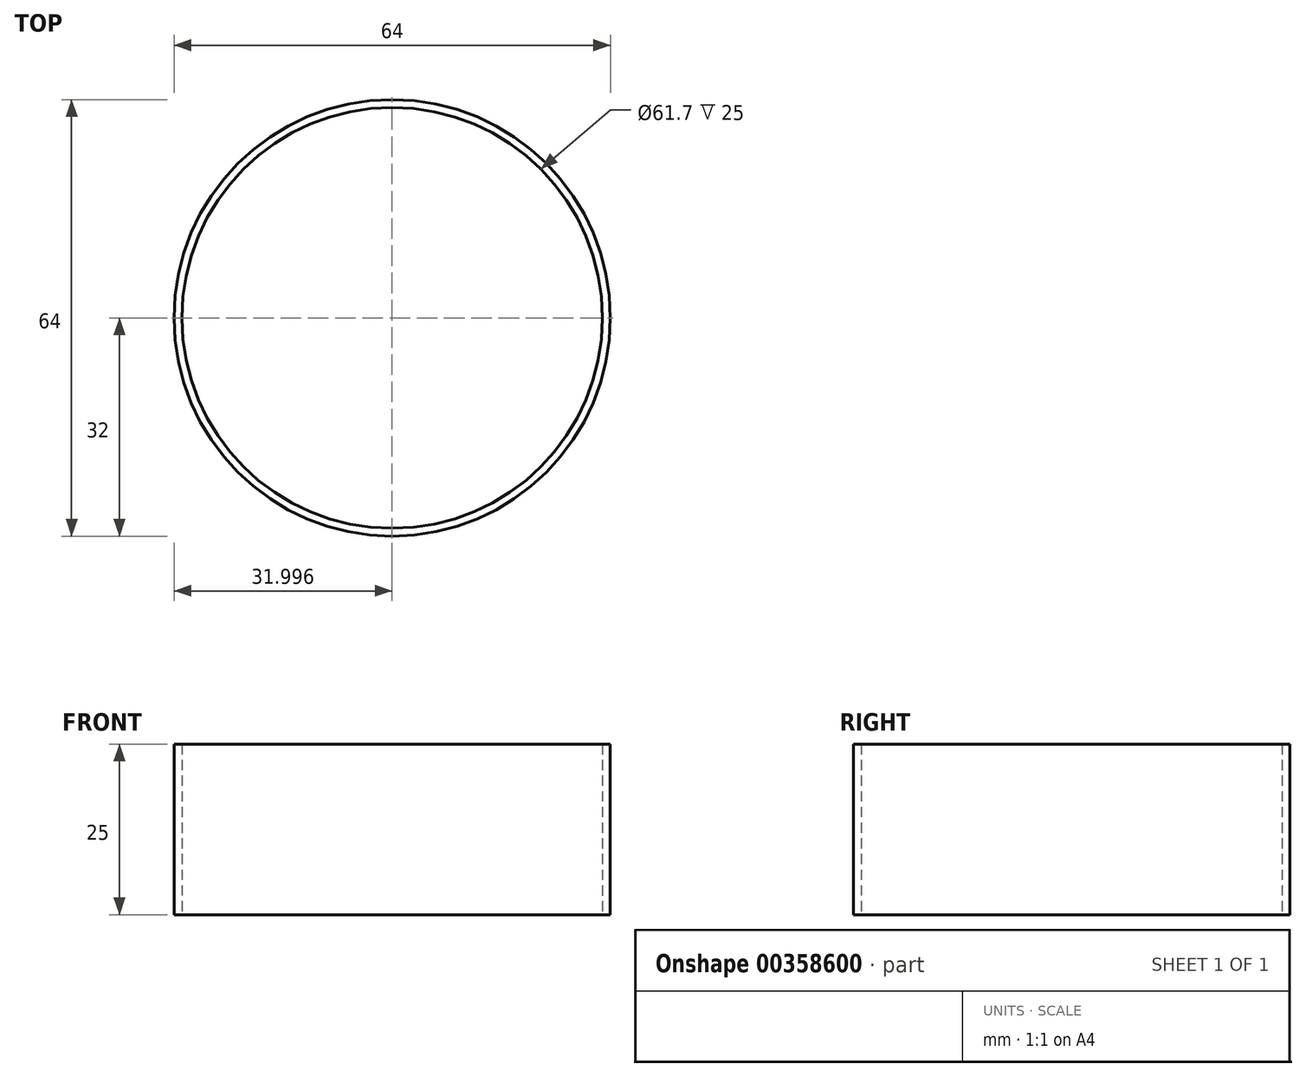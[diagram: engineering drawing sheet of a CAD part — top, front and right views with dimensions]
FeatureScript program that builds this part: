
annotation { "Feature Type Name" : "Feature", "Feature Type Description" : "" }
export const myFeature = defineFeature(function(context is Context, id is Id, definition is map)
    precondition{}
    {
        {
            var Q0;
            Q0=qCreatedBy(makeId("Top.planeOp"),FACE);
            var sketch = newSketch(context, id + "F0", { "sketchPlane" : qUnion([Q0])});
            skLineSegment(sketch, "E0", {"start": v(7.64, -19.63) * mm, "end": v(10.34, -16.68) * mm});
            skLineSegment(sketch, "E1", {"start": v(10.34, -16.68) * mm, "end": v(12.7, -18.83) * mm});
            skLineSegment(sketch, "E2", {"start": v(12.7, -18.83) * mm, "end": v(10, -21.79) * mm});
            skLineSegment(sketch, "E3", {"start": v(10, -21.79) * mm, "end": v(10.96, -22.66) * mm});
            skLineSegment(sketch, "E4", {"start": v(10.96, -22.66) * mm, "end": v(14.34, -18.97) * mm});
            skLineSegment(sketch, "E5", {"start": v(14.34, -18.97) * mm, "end": v(17.44, -21.8) * mm});
            skLineSegment(sketch, "E6", {"start": v(17.44, -21.8) * mm, "end": v(11.23, -28.6) * mm});
            skLineSegment(sketch, "E7", {"start": v(11.23, -28.6) * mm, "end": v(0.75, -19.02) * mm});
            skLineSegment(sketch, "E8", {"start": v(0.75, -19.02) * mm, "end": v(3.58, -15.92) * mm});
            skLineSegment(sketch, "E9", {"start": v(3.58, -15.92) * mm, "end": v(7.64, -19.63) * mm});
            skLineSegment(sketch, "E10", {"start": v(11.3, -18.9) * mm, "end": v(8.6, -21.85) * mm});
            skLineSegment(sketch, "E11", {"start": v(8.6, -21.85) * mm, "end": v(11.03, -24.08) * mm});
            skLineSegment(sketch, "E12", {"start": v(11.03, -24.08) * mm, "end": v(14.4, -20.39) * mm});
            skLineSegment(sketch, "E13", {"start": v(14.4, -20.39) * mm, "end": v(16.02, -21.87) * mm});
            skLineSegment(sketch, "E14", {"start": v(16.02, -21.87) * mm, "end": v(11.17, -27.18) * mm});
            skLineSegment(sketch, "E15", {"start": v(11.17, -27.18) * mm, "end": v(2.16, -18.95) * mm});
            skLineSegment(sketch, "E16", {"start": v(2.16, -18.95) * mm, "end": v(3.65, -17.33) * mm});
            skLineSegment(sketch, "E17", {"start": v(3.65, -17.33) * mm, "end": v(7.7, -21.04) * mm});
            skLineSegment(sketch, "E18", {"start": v(7.7, -21.04) * mm, "end": v(10.4, -18.09) * mm});
            skLineSegment(sketch, "E19", {"start": v(10.4, -18.09) * mm, "end": v(11.3, -18.9) * mm});
            skLineSegment(sketch, "E20", {"start": v(19.9, -16.36) * mm, "end": v(6.3, -12.26) * mm});
            skLineSegment(sketch, "E21", {"start": v(6.3, -12.26) * mm, "end": v(7.5, -8.24) * mm});
            skLineSegment(sketch, "E22", {"start": v(7.5, -8.24) * mm, "end": v(21.1, -12.34) * mm});
            skLineSegment(sketch, "E23", {"start": v(21.1, -12.34) * mm, "end": v(19.9, -16.36) * mm});
            skLineSegment(sketch, "E24", {"start": v(8.18, -9.49) * mm, "end": v(19.86, -13.01) * mm});
            skLineSegment(sketch, "E25", {"start": v(19.86, -13.01) * mm, "end": v(19.22, -15.12) * mm});
            skLineSegment(sketch, "E26", {"start": v(19.22, -15.12) * mm, "end": v(7.54, -11.6) * mm});
            skLineSegment(sketch, "E27", {"start": v(7.54, -11.6) * mm, "end": v(8.18, -9.49) * mm});
            skLineSegment(sketch, "E28", {"start": v(8.58, -7.66) * mm, "end": v(7.26, -3.4) * mm});
            skLineSegment(sketch, "E29", {"start": v(7.26, -3.4) * mm, "end": v(9.4, -1.36) * mm});
            skLineSegment(sketch, "E30", {"start": v(9.4, -1.36) * mm, "end": v(6.48, -0.88) * mm});
            skLineSegment(sketch, "E31", {"start": v(6.48, -0.88) * mm, "end": v(5.17, 3.38) * mm});
            skLineSegment(sketch, "E32", {"start": v(5.17, 3.38) * mm, "end": v(13, 2.08) * mm});
            skLineSegment(sketch, "E33", {"start": v(13, 2.08) * mm, "end": v(18.74, 7.57) * mm});
            skLineSegment(sketch, "E34", {"start": v(18.74, 7.57) * mm, "end": v(20.05, 3.3) * mm});
            skLineSegment(sketch, "E35", {"start": v(20.05, 3.3) * mm, "end": v(17.92, 1.27) * mm});
            skLineSegment(sketch, "E36", {"start": v(17.92, 1.27) * mm, "end": v(20.83, 0.78) * mm});
            skLineSegment(sketch, "E37", {"start": v(20.83, 0.78) * mm, "end": v(22.14, -3.48) * mm});
            skLineSegment(sketch, "E38", {"start": v(22.14, -3.48) * mm, "end": v(14.31, -2.18) * mm});
            skLineSegment(sketch, "E39", {"start": v(14.31, -2.18) * mm, "end": v(8.58, -7.66) * mm});
            skLineSegment(sketch, "E40", {"start": v(11.53, -0.7) * mm, "end": v(7.26, 0) * mm});
            skLineSegment(sketch, "E41", {"start": v(7.26, 0) * mm, "end": v(6.6, 2.13) * mm});
            skLineSegment(sketch, "E42", {"start": v(6.6, 2.13) * mm, "end": v(13.33, 1.01) * mm});
            skLineSegment(sketch, "E43", {"start": v(13.33, 1.01) * mm, "end": v(18.26, 5.73) * mm});
            skLineSegment(sketch, "E44", {"start": v(18.26, 5.73) * mm, "end": v(18.91, 3.6) * mm});
            skLineSegment(sketch, "E45", {"start": v(18.91, 3.6) * mm, "end": v(15.78, 0.6) * mm});
            skLineSegment(sketch, "E46", {"start": v(15.78, 0.6) * mm, "end": v(20.06, -0.1) * mm});
            skLineSegment(sketch, "E47", {"start": v(20.06, -0.1) * mm, "end": v(20.71, -2.23) * mm});
            skLineSegment(sketch, "E48", {"start": v(20.71, -2.23) * mm, "end": v(13.98, -1.11) * mm});
            skLineSegment(sketch, "E49", {"start": v(13.98, -1.11) * mm, "end": v(9.05, -5.82) * mm});
            skLineSegment(sketch, "E50", {"start": v(9.05, -5.82) * mm, "end": v(8.4, -3.7) * mm});
            skLineSegment(sketch, "E51", {"start": v(8.4, -3.7) * mm, "end": v(11.53, -0.7) * mm});
            skLineSegment(sketch, "E52", {"start": v(2.47, 9.54) * mm, "end": v(3.08, 10.69) * mm});
            skLineSegment(sketch, "E53", {"start": v(3.08, 10.69) * mm, "end": v(0.43, 12.1) * mm});
            skLineSegment(sketch, "E54", {"start": v(0.43, 12.1) * mm, "end": v(1.94, 14.92) * mm});
            skLineSegment(sketch, "E55", {"start": v(1.94, 14.92) * mm, "end": v(4.59, 13.51) * mm});
            skLineSegment(sketch, "E56", {"start": v(4.59, 13.51) * mm, "end": v(5.2, 14.66) * mm});
            skLineSegment(sketch, "E57", {"start": v(5.2, 14.66) * mm, "end": v(0.79, 17.01) * mm});
            skLineSegment(sketch, "E58", {"start": v(0.79, 17.01) * mm, "end": v(2.76, 20.72) * mm});
            skLineSegment(sketch, "E59", {"start": v(2.76, 20.72) * mm, "end": v(10.88, 16.39) * mm});
            skLineSegment(sketch, "E60", {"start": v(10.88, 16.39) * mm, "end": v(4.2, 3.86) * mm});
            skLineSegment(sketch, "E61", {"start": v(4.2, 3.86) * mm, "end": v(-3.92, 8.19) * mm});
            skLineSegment(sketch, "E62", {"start": v(-3.92, 8.19) * mm, "end": v(-1.94, 11.9) * mm});
            skLineSegment(sketch, "E63", {"start": v(-1.94, 11.9) * mm, "end": v(2.47, 9.54) * mm});
            skLineSegment(sketch, "E64", {"start": v(1.79, 12.51) * mm, "end": v(2.35, 13.57) * mm});
            skLineSegment(sketch, "E65", {"start": v(2.35, 13.57) * mm, "end": v(5, 12.16) * mm});
            skLineSegment(sketch, "E66", {"start": v(5, 12.16) * mm, "end": v(6.55, 15.07) * mm});
            skLineSegment(sketch, "E67", {"start": v(6.55, 15.07) * mm, "end": v(2.14, 17.42) * mm});
            skLineSegment(sketch, "E68", {"start": v(2.14, 17.42) * mm, "end": v(3.18, 19.36) * mm});
            skLineSegment(sketch, "E69", {"start": v(3.18, 19.36) * mm, "end": v(9.53, 15.98) * mm});
            skLineSegment(sketch, "E70", {"start": v(9.53, 15.98) * mm, "end": v(3.79, 5.21) * mm});
            skLineSegment(sketch, "E71", {"start": v(3.79, 5.21) * mm, "end": v(-2.57, 8.6) * mm});
            skLineSegment(sketch, "E72", {"start": v(-2.57, 8.6) * mm, "end": v(-1.53, 10.54) * mm});
            skLineSegment(sketch, "E73", {"start": v(-1.53, 10.54) * mm, "end": v(2.88, 8.19) * mm});
            skLineSegment(sketch, "E74", {"start": v(2.88, 8.19) * mm, "end": v(4.43, 11.1) * mm});
            skLineSegment(sketch, "E75", {"start": v(4.43, 11.1) * mm, "end": v(1.79, 12.51) * mm});
            skLineSegment(sketch, "E76", {"start": v(-5.9, 21.93) * mm, "end": v(-5.4, 12.94) * mm});
            skLineSegment(sketch, "E77", {"start": v(-5.4, 12.94) * mm, "end": v(-9.59, 12.7) * mm});
            skLineSegment(sketch, "E78", {"start": v(-9.59, 12.7) * mm, "end": v(-10.1, 21.7) * mm});
            skLineSegment(sketch, "E79", {"start": v(-10.1, 21.7) * mm, "end": v(-5.9, 21.93) * mm});
            skLineSegment(sketch, "E80", {"start": v(-5.33, 11.76) * mm, "end": v(-5.1, 7.76) * mm});
            skLineSegment(sketch, "E81", {"start": v(-5.1, 7.76) * mm, "end": v(-9.3, 7.52) * mm});
            skLineSegment(sketch, "E82", {"start": v(-9.3, 7.52) * mm, "end": v(-9.52, 11.52) * mm});
            skLineSegment(sketch, "E83", {"start": v(-9.52, 11.52) * mm, "end": v(-5.33, 11.76) * mm});
            skLineSegment(sketch, "E84", {"start": v(-8.65, 13.76) * mm, "end": v(-9.05, 20.75) * mm});
            skLineSegment(sketch, "E85", {"start": v(-9.05, 20.75) * mm, "end": v(-6.85, 20.88) * mm});
            skLineSegment(sketch, "E86", {"start": v(-6.85, 20.88) * mm, "end": v(-6.45, 13.88) * mm});
            skLineSegment(sketch, "E87", {"start": v(-6.45, 13.88) * mm, "end": v(-8.65, 13.76) * mm});
            skArc(sketch, "E88", {"start": v(-13.06, 18.5) * mm, "mid": v(-14, 19.26) * mm, "end": v(-15.15, 19.61) * mm});
            skArc(sketch, "E89", {"start": v(-12.28, 16.43) * mm, "mid": v(-12.52, 17.52) * mm, "end": v(-13.06, 18.5) * mm});
            skArc(sketch, "E90", {"start": v(-12.46, 13.44) * mm, "mid": v(-12.26, 14.93) * mm, "end": v(-12.28, 16.43) * mm});
            skArc(sketch, "E91", {"start": v(-12.66, 12.24) * mm, "mid": v(-12.54, 12.84) * mm, "end": v(-12.46, 13.44) * mm});
            skArc(sketch, "E92", {"start": v(-13.27, 9.68) * mm, "mid": v(-12.94, 10.95) * mm, "end": v(-12.66, 12.24) * mm});
            skArc(sketch, "E93", {"start": v(-13.72, 7.8) * mm, "mid": v(-13.49, 8.74) * mm, "end": v(-13.27, 9.68) * mm});
            skArc(sketch, "E94", {"start": v(-13.72, 7.8) * mm, "mid": v(-13.93, 6.87) * mm, "end": v(-14.07, 5.93) * mm});
            skArc(sketch, "E95", {"start": v(-14.07, 5.93) * mm, "mid": v(-14.27, 3.78) * mm, "end": v(-14.07, 1.63) * mm});
            skArc(sketch, "E96", {"start": v(-14.07, 1.63) * mm, "mid": v(-13.07, 1.3) * mm, "end": v(-12.06, 0.96) * mm});
            skArc(sketch, "E97", {"start": v(-9.78, -0.07) * mm, "mid": v(-10.9, 0.5) * mm, "end": v(-12.06, 0.96) * mm});
            skArc(sketch, "E98", {"start": v(-8.8, -1.07) * mm, "mid": v(-9.2, -0.49) * mm, "end": v(-9.78, -0.07) * mm});
            skArc(sketch, "E99", {"start": v(-8.35, -3.1) * mm, "mid": v(-8.45, -2.07) * mm, "end": v(-8.8, -1.07) * mm});
            skArc(sketch, "E100", {"start": v(-8.93, -4.22) * mm, "mid": v(-8.6, -3.68) * mm, "end": v(-8.35, -3.1) * mm});
            skArc(sketch, "E101", {"start": v(-8.93, -4.22) * mm, "mid": v(-9.21, -4.72) * mm, "end": v(-9.42, -5.26) * mm});
            skArc(sketch, "E102", {"start": v(-9.42, -5.26) * mm, "mid": v(-9.41, -5.63) * mm, "end": v(-9.25, -5.96) * mm});
            skArc(sketch, "E103", {"start": v(-9.25, -5.96) * mm, "mid": v(-8.9, -6.42) * mm, "end": v(-8.53, -6.87) * mm});
            skArc(sketch, "E104", {"start": v(-7.87, -8.12) * mm, "mid": v(-8.1, -7.45) * mm, "end": v(-8.53, -6.87) * mm});
            skArc(sketch, "E105", {"start": v(-8.17, -9.55) * mm, "mid": v(-7.9, -8.86) * mm, "end": v(-7.87, -8.12) * mm});
            skArc(sketch, "E106", {"start": v(-9.14, -10.66) * mm, "mid": v(-8.63, -10.12) * mm, "end": v(-8.17, -9.55) * mm});
            skArc(sketch, "E107", {"start": v(-9.14, -10.66) * mm, "mid": v(-9.58, -11.15) * mm, "end": v(-9.96, -11.7) * mm});
            skArc(sketch, "E108", {"start": v(-9.96, -11.7) * mm, "mid": v(-9.44, -12.78) * mm, "end": v(-8.89, -13.84) * mm});
            skArc(sketch, "E109", {"start": v(-8.88, -13.84) * mm, "mid": v(-8.2, -14.64) * mm, "end": v(-7.45, -15.36) * mm});
            skArc(sketch, "E110", {"start": v(-7.45, -15.36) * mm, "mid": v(-6.66, -16.01) * mm, "end": v(-5.84, -16.62) * mm});
            skArc(sketch, "E111", {"start": v(-5.84, -16.62) * mm, "mid": v(-4.74, -17.36) * mm, "end": v(-3.5, -17.85) * mm});
            skArc(sketch, "E112", {"start": v(-1.55, -18.5) * mm, "mid": v(-2.51, -18.15) * mm, "end": v(-3.5, -17.85) * mm});
            skArc(sketch, "E113", {"start": v(0.15, -20.57) * mm, "mid": v(-0.58, -19.44) * mm, "end": v(-1.55, -18.5) * mm});
            skArc(sketch, "E114", {"start": v(0.78, -22.16) * mm, "mid": v(0.5, -21.35) * mm, "end": v(0.15, -20.57) * mm});
            skArc(sketch, "E115", {"start": v(0.69, -26.46) * mm, "mid": v(0.98, -24.31) * mm, "end": v(0.78, -22.16) * mm});
            skArc(sketch, "E116", {"start": v(-2.62, -31.64) * mm, "mid": v(-0.48, -29.36) * mm, "end": v(0.69, -26.46) * mm});
            skArc(sketch, "E117", {"start": v(-4.33, -32.6) * mm, "mid": v(-3.46, -32.16) * mm, "end": v(-2.62, -31.64) * mm});
            skArc(sketch, "E118", {"start": v(-5.84, -33.25) * mm, "mid": v(-5.09, -32.93) * mm, "end": v(-4.33, -32.6) * mm});
            skArc(sketch, "E119", {"start": v(-8.1, -33.86) * mm, "mid": v(-6.96, -33.61) * mm, "end": v(-5.84, -33.25) * mm});
            skArc(sketch, "E120", {"start": v(-10.67, -33.52) * mm, "mid": v(-9.42, -33.88) * mm, "end": v(-8.1, -33.86) * mm});
            skArc(sketch, "E121", {"start": v(-12.25, -31.6) * mm, "mid": v(-11.56, -32.64) * mm, "end": v(-10.67, -33.52) * mm});
            skArc(sketch, "E122", {"start": v(-12.25, -31.6) * mm, "mid": v(-12.77, -30.65) * mm, "end": v(-13.3, -29.7) * mm});
            skArc(sketch, "E123", {"start": v(-13.3, -29.7) * mm, "mid": v(-14.03, -28.7) * mm, "end": v(-14.97, -27.89) * mm});
            skArc(sketch, "E124", {"start": v(-14.97, -27.89) * mm, "mid": v(-15.8, -27.66) * mm, "end": v(-16.64, -27.57) * mm});
            skArc(sketch, "E125", {"start": v(-18.32, -27.51) * mm, "mid": v(-17.48, -27.55) * mm, "end": v(-16.64, -27.57) * mm});
            skArc(sketch, "E126", {"start": v(-20.33, -26.81) * mm, "mid": v(-19.38, -27.3) * mm, "end": v(-18.32, -27.51) * mm});
            skArc(sketch, "E127", {"start": v(-21.17, -25.98) * mm, "mid": v(-20.8, -26.45) * mm, "end": v(-20.33, -26.81) * mm});
            skArc(sketch, "E128", {"start": v(-21.17, -25.98) * mm, "mid": v(-21.45, -25.54) * mm, "end": v(-21.76, -25.13) * mm});
            skArc(sketch, "E129", {"start": v(-21.76, -25.13) * mm, "mid": v(-22.13, -24.88) * mm, "end": v(-22.57, -24.85) * mm});
            skArc(sketch, "E130", {"start": v(-24.43, -24.44) * mm, "mid": v(-23.5, -24.67) * mm, "end": v(-22.57, -24.85) * mm});
            skArc(sketch, "E131", {"start": v(-24.72, -24.3) * mm, "mid": v(-24.58, -24.4) * mm, "end": v(-24.43, -24.44) * mm});
            skArc(sketch, "E132", {"start": v(-26.05, -23.78) * mm, "mid": v(-25.4, -24.1) * mm, "end": v(-24.72, -24.3) * mm});
            skArc(sketch, "E133", {"start": v(-28.83, -21.18) * mm, "mid": v(-27.58, -22.63) * mm, "end": v(-26.05, -23.78) * mm});
            skArc(sketch, "E134", {"start": v(-29.33, -19.37) * mm, "mid": v(-29.3, -20.33) * mm, "end": v(-28.83, -21.18) * mm});
            skArc(sketch, "E135", {"start": v(-29.01, -17.96) * mm, "mid": v(-29.17, -18.66) * mm, "end": v(-29.33, -19.37) * mm});
            skArc(sketch, "E136", {"start": v(-29.78, -16.33) * mm, "mid": v(-29.54, -17.2) * mm, "end": v(-29.01, -17.96) * mm});
            skArc(sketch, "E137", {"start": v(-29.7, -14.25) * mm, "mid": v(-29.82, -15.29) * mm, "end": v(-29.78, -16.33) * mm});
            skArc(sketch, "E138", {"start": v(-29.7, -14.25) * mm, "mid": v(-29.66, -13.96) * mm, "end": v(-29.64, -13.66) * mm});
            skArc(sketch, "E139", {"start": v(-29.64, -13.66) * mm, "mid": v(-29.82, -13.43) * mm, "end": v(-30.06, -13.25) * mm});
            skArc(sketch, "E140", {"start": v(-30.53, -12.77) * mm, "mid": v(-30.34, -13.05) * mm, "end": v(-30.06, -13.25) * mm});
            skArc(sketch, "E141", {"start": v(-31.7, -7.94) * mm, "mid": v(-31.47, -10.44) * mm, "end": v(-30.53, -12.77) * mm});
            skArc(sketch, "E142", {"start": v(-31.24, -6.93) * mm, "mid": v(-31.53, -7.4) * mm, "end": v(-31.7, -7.94) * mm});
            skArc(sketch, "E143", {"start": v(-31.24, -6.93) * mm, "mid": v(-30.86, -6.38) * mm, "end": v(-30.53, -5.8) * mm});
            skArc(sketch, "E144", {"start": v(-30.51, -3.03) * mm, "mid": v(-30.72, -4.4) * mm, "end": v(-30.53, -5.8) * mm});
            skArc(sketch, "E145", {"start": v(-29.28, -0.43) * mm, "mid": v(-29.99, -1.68) * mm, "end": v(-30.51, -3.03) * mm});
            skArc(sketch, "E146", {"start": v(-29.28, -0.43) * mm, "mid": v(-28.65, 0.5) * mm, "end": v(-28.03, 1.4) * mm});
            skArc(sketch, "E147", {"start": v(-26.33, 3.24) * mm, "mid": v(-27.25, 2.39) * mm, "end": v(-28.03, 1.4) * mm});
            skArc(sketch, "E148", {"start": v(-24.86, 3.63) * mm, "mid": v(-25.62, 3.54) * mm, "end": v(-26.33, 3.24) * mm});
            skArc(sketch, "E149", {"start": v(-23.63, 3.52) * mm, "mid": v(-24.24, 3.6) * mm, "end": v(-24.86, 3.63) * mm});
            skArc(sketch, "E150", {"start": v(-23.63, 3.52) * mm, "mid": v(-23.1, 3.45) * mm, "end": v(-22.57, 3.42) * mm});
            skArc(sketch, "E151", {"start": v(-22.57, 3.42) * mm, "mid": v(-22.43, 3.4) * mm, "end": v(-22.35, 3.52) * mm});
            skArc(sketch, "E152", {"start": v(-22.35, 3.52) * mm, "mid": v(-22.3, 3.9) * mm, "end": v(-22.31, 4.28) * mm});
            skArc(sketch, "E153", {"start": v(-22.31, 4.28) * mm, "mid": v(-22.49, 5.6) * mm, "end": v(-22.75, 6.9) * mm});
            skArc(sketch, "E154", {"start": v(-23.2, 9.32) * mm, "mid": v(-23.02, 8.1) * mm, "end": v(-22.75, 6.9) * mm});
            skArc(sketch, "E155", {"start": v(-23.2, 11.74) * mm, "mid": v(-23.28, 10.53) * mm, "end": v(-23.2, 9.32) * mm});
            skArc(sketch, "E156", {"start": v(-22.16, 14.77) * mm, "mid": v(-22.78, 13.3) * mm, "end": v(-23.2, 11.74) * mm});
            skArc(sketch, "E157", {"start": v(-19.44, 18) * mm, "mid": v(-20.99, 16.55) * mm, "end": v(-22.16, 14.77) * mm});
            skArc(sketch, "E158", {"start": v(-17.62, 19.25) * mm, "mid": v(-18.59, 18.7) * mm, "end": v(-19.44, 18) * mm});
            skArc(sketch, "E159", {"start": v(-15.15, 19.61) * mm, "mid": v(-16.4, 19.6) * mm, "end": v(-17.62, 19.25) * mm});
            skArc(sketch, "E160", {"start": v(-16.85, 18.63) * mm, "mid": v(-19.9, 16.4) * mm, "end": v(-21.83, 13.14) * mm});
            skArc(sketch, "E161", {"start": v(-21.83, 13.14) * mm, "mid": v(-22.26, 11.48) * mm, "end": v(-22.4, 9.77) * mm});
            skArc(sketch, "E162", {"start": v(-22.4, 9.77) * mm, "mid": v(-22.12, 8.15) * mm, "end": v(-21.78, 6.55) * mm});
            skArc(sketch, "E163", {"start": v(-21.4, 3.33) * mm, "mid": v(-21.5, 4.95) * mm, "end": v(-21.78, 6.55) * mm});
            skArc(sketch, "E164", {"start": v(-21.4, 3.33) * mm, "mid": v(-20.07, 3.03) * mm, "end": v(-18.73, 2.78) * mm});
            skArc(sketch, "E165", {"start": v(-16.04, 2.17) * mm, "mid": v(-17.37, 2.5) * mm, "end": v(-18.72, 2.78) * mm});
            skArc(sketch, "E166", {"start": v(-15.24, 1.94) * mm, "mid": v(-15.64, 2.06) * mm, "end": v(-16.04, 2.17) * mm});
            skArc(sketch, "E167", {"start": v(-15.24, 1.94) * mm, "mid": v(-15.14, 1.93) * mm, "end": v(-15.06, 1.99) * mm});
            skArc(sketch, "E168", {"start": v(-15.14, 4.4) * mm, "mid": v(-15.15, 3.2) * mm, "end": v(-15.06, 1.99) * mm});
            skArc(sketch, "E169", {"start": v(-14.88, 6.82) * mm, "mid": v(-15.04, 5.62) * mm, "end": v(-15.14, 4.4) * mm});
            skArc(sketch, "E170", {"start": v(-14.88, 6.82) * mm, "mid": v(-14.55, 8.16) * mm, "end": v(-14.25, 9.5) * mm});
            skArc(sketch, "E171", {"start": v(-14.25, 9.5) * mm, "mid": v(-13.91, 10.7) * mm, "end": v(-13.65, 11.92) * mm});
            skArc(sketch, "E172", {"start": v(-13.18, 14.33) * mm, "mid": v(-13.42, 13.13) * mm, "end": v(-13.65, 11.92) * mm});
            skArc(sketch, "E173", {"start": v(-13.18, 15.92) * mm, "mid": v(-13.19, 15.13) * mm, "end": v(-13.18, 14.33) * mm});
            skArc(sketch, "E174", {"start": v(-13.18, 15.92) * mm, "mid": v(-13.41, 17.1) * mm, "end": v(-14.07, 18.1) * mm});
            skArc(sketch, "E175", {"start": v(-14.07, 18.1) * mm, "mid": v(-14.86, 18.57) * mm, "end": v(-15.76, 18.73) * mm});
            skArc(sketch, "E176", {"start": v(-15.76, 18.73) * mm, "mid": v(-16.3, 18.7) * mm, "end": v(-16.85, 18.63) * mm});
            skArc(sketch, "E177", {"start": v(-24.99, 2.7) * mm, "mid": v(-25.3, 2.67) * mm, "end": v(-25.6, 2.53) * mm});
            skArc(sketch, "E178", {"start": v(-25.6, 2.53) * mm, "mid": v(-26.1, 2.14) * mm, "end": v(-26.54, 1.7) * mm});
            skArc(sketch, "E179", {"start": v(-26.54, 1.7) * mm, "mid": v(-28.26, -0.66) * mm, "end": v(-29.54, -3.27) * mm});
            skArc(sketch, "E180", {"start": v(-29.54, -3.27) * mm, "mid": v(-29.74, -3.94) * mm, "end": v(-29.82, -4.63) * mm});
            skArc(sketch, "E181", {"start": v(-29.82, -4.63) * mm, "mid": v(-29.82, -4.79) * mm, "end": v(-29.8, -4.95) * mm});
            skArc(sketch, "E182", {"start": v(-29.8, -4.95) * mm, "mid": v(-29.7, -4.9) * mm, "end": v(-29.64, -4.8) * mm});
            skArc(sketch, "E183", {"start": v(-28.22, -3.45) * mm, "mid": v(-29.01, -4.05) * mm, "end": v(-29.64, -4.8) * mm});
            skArc(sketch, "E184", {"start": v(-26.4, -2.94) * mm, "mid": v(-27.34, -3.1) * mm, "end": v(-28.22, -3.45) * mm});
            skArc(sketch, "E185", {"start": v(-24.9, -2.93) * mm, "mid": v(-25.65, -2.92) * mm, "end": v(-26.4, -2.94) * mm});
            skArc(sketch, "E186", {"start": v(-22.21, -3.2) * mm, "mid": v(-23.55, -3.05) * mm, "end": v(-24.9, -2.93) * mm});
            skArc(sketch, "E187", {"start": v(-18.46, -3.82) * mm, "mid": v(-20.32, -3.41) * mm, "end": v(-22.21, -3.2) * mm});
            skArc(sketch, "E188", {"start": v(-18.46, -3.82) * mm, "mid": v(-17.48, -4.11) * mm, "end": v(-16.46, -4.16) * mm});
            skArc(sketch, "E189", {"start": v(-16.46, -4.16) * mm, "mid": v(-15.58, -4.07) * mm, "end": v(-14.7, -3.91) * mm});
            skArc(sketch, "E190", {"start": v(-14.54, -4.14) * mm, "mid": v(-14.6, -4.02) * mm, "end": v(-14.7, -3.91) * mm});
            skArc(sketch, "E191", {"start": v(-14.46, -4.71) * mm, "mid": v(-14.46, -4.42) * mm, "end": v(-14.54, -4.14) * mm});
            skArc(sketch, "E192", {"start": v(-14.7, -4.9) * mm, "mid": v(-14.54, -4.85) * mm, "end": v(-14.46, -4.71) * mm});
            skArc(sketch, "E193", {"start": v(-14.7, -4.9) * mm, "mid": v(-15.37, -5.04) * mm, "end": v(-16.04, -5.2) * mm});
            skArc(sketch, "E194", {"start": v(-17.38, -5.17) * mm, "mid": v(-16.71, -5.27) * mm, "end": v(-16.04, -5.2) * mm});
            skArc(sketch, "E195", {"start": v(-19.26, -4.74) * mm, "mid": v(-18.33, -4.98) * mm, "end": v(-17.38, -5.17) * mm});
            skArc(sketch, "E196", {"start": v(-19.26, -4.74) * mm, "mid": v(-20.2, -4.49) * mm, "end": v(-21.14, -4.27) * mm});
            skArc(sketch, "E197", {"start": v(-21.14, -4.27) * mm, "mid": v(-22.61, -4.11) * mm, "end": v(-24.1, -4.01) * mm});
            skArc(sketch, "E198", {"start": v(-24.1, -4.01) * mm, "mid": v(-25.57, -4) * mm, "end": v(-27.04, -4.1) * mm});
            skArc(sketch, "E199", {"start": v(-27.04, -4.1) * mm, "mid": v(-27.27, -4.2) * mm, "end": v(-27.49, -4.35) * mm});
            skArc(sketch, "E200", {"start": v(-27.49, -4.35) * mm, "mid": v(-28.37, -5.08) * mm, "end": v(-29.2, -5.88) * mm});
            skArc(sketch, "E201", {"start": v(-29.2, -5.88) * mm, "mid": v(-29.98, -6.66) * mm, "end": v(-30.57, -7.6) * mm});
            skArc(sketch, "E202", {"start": v(-30.57, -7.6) * mm, "mid": v(-30.8, -8.29) * mm, "end": v(-30.8, -9.01) * mm});
            skArc(sketch, "E203", {"start": v(-30.8, -9.01) * mm, "mid": v(-30.56, -10.39) * mm, "end": v(-30.09, -11.7) * mm});
            skArc(sketch, "E204", {"start": v(-30.09, -11.7) * mm, "mid": v(-29.92, -12.09) * mm, "end": v(-29.65, -12.42) * mm});
            skArc(sketch, "E205", {"start": v(-29.65, -12.42) * mm, "mid": v(-29.46, -12.5) * mm, "end": v(-29.28, -12.41) * mm});
            skArc(sketch, "E206", {"start": v(-27.7, -10.7) * mm, "mid": v(-28.58, -11.47) * mm, "end": v(-29.28, -12.41) * mm});
            skArc(sketch, "E207", {"start": v(-26.86, -10.27) * mm, "mid": v(-27.3, -10.45) * mm, "end": v(-27.7, -10.7) * mm});
            skArc(sketch, "E208", {"start": v(-23.38, -10.08) * mm, "mid": v(-25.12, -10.1) * mm, "end": v(-26.86, -10.27) * mm});
            skArc(sketch, "E209", {"start": v(-19.89, -10.27) * mm, "mid": v(-21.63, -10.16) * mm, "end": v(-23.38, -10.08) * mm});
            skArc(sketch, "E210", {"start": v(-19.88, -10.26) * mm, "mid": v(-17.74, -10.5) * mm, "end": v(-15.6, -10.71) * mm});
            skArc(sketch, "E211", {"start": v(-15.46, -10.89) * mm, "mid": v(-15.51, -10.79) * mm, "end": v(-15.6, -10.71) * mm});
            skArc(sketch, "E212", {"start": v(-15.55, -11.6) * mm, "mid": v(-15.44, -11.25) * mm, "end": v(-15.46, -10.89) * mm});
            skArc(sketch, "E213", {"start": v(-15.68, -11.7) * mm, "mid": v(-15.6, -11.66) * mm, "end": v(-15.55, -11.6) * mm});
            skArc(sketch, "E214", {"start": v(-15.68, -11.7) * mm, "mid": v(-16.62, -11.59) * mm, "end": v(-17.56, -11.52) * mm});
            skArc(sketch, "E215", {"start": v(-19.44, -11.34) * mm, "mid": v(-18.5, -11.45) * mm, "end": v(-17.56, -11.52) * mm});
            skArc(sketch, "E216", {"start": v(-19.44, -11.34) * mm, "mid": v(-21.18, -11.24) * mm, "end": v(-22.93, -11.18) * mm});
            skArc(sketch, "E217", {"start": v(-22.93, -11.18) * mm, "mid": v(-24.67, -11.17) * mm, "end": v(-26.42, -11.25) * mm});
            skArc(sketch, "E218", {"start": v(-26.42, -11.25) * mm, "mid": v(-26.9, -11.48) * mm, "end": v(-27.32, -11.8) * mm});
            skArc(sketch, "E219", {"start": v(-27.32, -11.8) * mm, "mid": v(-27.95, -12.42) * mm, "end": v(-28.56, -13.04) * mm});
            skArc(sketch, "E220", {"start": v(-28.56, -13.04) * mm, "mid": v(-28.76, -13.84) * mm, "end": v(-28.92, -14.65) * mm});
            skArc(sketch, "E221", {"start": v(-28.92, -15.48) * mm, "mid": v(-28.9, -15.06) * mm, "end": v(-28.92, -14.65) * mm});
            skArc(sketch, "E222", {"start": v(-28.92, -15.48) * mm, "mid": v(-28.92, -15.93) * mm, "end": v(-28.88, -16.39) * mm});
            skArc(sketch, "E223", {"start": v(-28.88, -16.39) * mm, "mid": v(-28.71, -16.86) * mm, "end": v(-28.39, -17.24) * mm});
            skArc(sketch, "E224", {"start": v(-26.46, -16.88) * mm, "mid": v(-27.45, -16.93) * mm, "end": v(-28.39, -17.24) * mm});
            skArc(sketch, "E225", {"start": v(-24.7, -17.12) * mm, "mid": v(-25.57, -16.98) * mm, "end": v(-26.46, -16.88) * mm});
            skArc(sketch, "E226", {"start": v(-24.7, -17.12) * mm, "mid": v(-23.86, -17.2) * mm, "end": v(-23.02, -17.15) * mm});
            skArc(sketch, "E227", {"start": v(-23.02, -17.15) * mm, "mid": v(-21.81, -17.16) * mm, "end": v(-20.6, -17.1) * mm});
            skArc(sketch, "E228", {"start": v(-18.19, -16.97) * mm, "mid": v(-19.4, -17.02) * mm, "end": v(-20.6, -17.1) * mm});
            skArc(sketch, "E229", {"start": v(-18, -17.1) * mm, "mid": v(-18.08, -17.02) * mm, "end": v(-18.19, -16.97) * mm});
            skArc(sketch, "E230", {"start": v(-17.94, -17.74) * mm, "mid": v(-17.9, -17.41) * mm, "end": v(-18, -17.1) * mm});
            skArc(sketch, "E231", {"start": v(-18.1, -17.87) * mm, "mid": v(-18, -17.83) * mm, "end": v(-17.94, -17.74) * mm});
            skArc(sketch, "E232", {"start": v(-22.4, -18.32) * mm, "mid": v(-20.24, -18.11) * mm, "end": v(-18.1, -17.87) * mm});
            skArc(sketch, "E233", {"start": v(-25.08, -18.5) * mm, "mid": v(-23.73, -18.43) * mm, "end": v(-22.4, -18.32) * mm});
            skArc(sketch, "E234", {"start": v(-27.76, -18.32) * mm, "mid": v(-26.42, -18.49) * mm, "end": v(-25.08, -18.5) * mm});
            skArc(sketch, "E235", {"start": v(-27.76, -18.32) * mm, "mid": v(-27.98, -18.32) * mm, "end": v(-28.14, -18.48) * mm});
            skArc(sketch, "E236", {"start": v(-28.14, -18.48) * mm, "mid": v(-28.28, -18.8) * mm, "end": v(-28.39, -19.12) * mm});
            skArc(sketch, "E237", {"start": v(-28.39, -19.12) * mm, "mid": v(-28.5, -19.64) * mm, "end": v(-28.38, -20.16) * mm});
            skArc(sketch, "E238", {"start": v(-28.38, -20.16) * mm, "mid": v(-28.05, -20.73) * mm, "end": v(-27.67, -21.27) * mm});
            skArc(sketch, "E239", {"start": v(-27.67, -21.27) * mm, "mid": v(-26.44, -22.42) * mm, "end": v(-24.99, -23.29) * mm});
            skArc(sketch, "E240", {"start": v(-24.99, -23.29) * mm, "mid": v(-23.67, -23.73) * mm, "end": v(-22.3, -23.95) * mm});
            skArc(sketch, "E241", {"start": v(-22.3, -23.95) * mm, "mid": v(-21.77, -24.07) * mm, "end": v(-21.23, -24.1) * mm});
            skArc(sketch, "E242", {"start": v(-20.16, -24.22) * mm, "mid": v(-20.69, -24.13) * mm, "end": v(-21.23, -24.1) * mm});
            skArc(sketch, "E243", {"start": v(-20.16, -24.22) * mm, "mid": v(-18.99, -24.2) * mm, "end": v(-17.82, -24.16) * mm});
            skArc(sketch, "E244", {"start": v(-17.82, -24.16) * mm, "mid": v(-16.56, -24.03) * mm, "end": v(-15.33, -23.77) * mm});
            skArc(sketch, "E245", {"start": v(-15.33, -23.77) * mm, "mid": v(-14.65, -23.49) * mm, "end": v(-13.97, -23.2) * mm});
            skArc(sketch, "E246", {"start": v(-13.97, -23.2) * mm, "mid": v(-13.3, -22.8) * mm, "end": v(-12.73, -22.25) * mm});
            skArc(sketch, "E247", {"start": v(-12.73, -22.25) * mm, "mid": v(-12.64, -21.89) * mm, "end": v(-12.66, -21.51) * mm});
            skArc(sketch, "E248", {"start": v(-12.8, -20.8) * mm, "mid": v(-12.73, -21.16) * mm, "end": v(-12.66, -21.51) * mm});
            skArc(sketch, "E249", {"start": v(-12.73, -20.1) * mm, "mid": v(-12.81, -20.45) * mm, "end": v(-12.8, -20.8) * mm});
            skArc(sketch, "E250", {"start": v(-12.28, -19.2) * mm, "mid": v(-12.56, -19.63) * mm, "end": v(-12.73, -20.1) * mm});
            skArc(sketch, "E251", {"start": v(-11.1, -17.94) * mm, "mid": v(-11.7, -18.55) * mm, "end": v(-12.28, -19.2) * mm});
            skArc(sketch, "E252", {"start": v(-11.1, -17.94) * mm, "mid": v(-10.63, -17.44) * mm, "end": v(-10.23, -16.88) * mm});
            skArc(sketch, "E253", {"start": v(-10.23, -16.88) * mm, "mid": v(-10.06, -16.36) * mm, "end": v(-10.1, -15.81) * mm});
            skArc(sketch, "E254", {"start": v(-10.1, -15.81) * mm, "mid": v(-10.24, -15.27) * mm, "end": v(-10.4, -14.74) * mm});
            skArc(sketch, "E255", {"start": v(-11, -13.04) * mm, "mid": v(-10.74, -13.9) * mm, "end": v(-10.4, -14.74) * mm});
            skArc(sketch, "E256", {"start": v(-10.58, -10.98) * mm, "mid": v(-11.01, -11.96) * mm, "end": v(-11, -13.04) * mm});
            skArc(sketch, "E257", {"start": v(-9.73, -9.97) * mm, "mid": v(-10.18, -10.46) * mm, "end": v(-10.58, -10.98) * mm});
            skArc(sketch, "E258", {"start": v(-9.73, -9.97) * mm, "mid": v(-9.3, -9.51) * mm, "end": v(-8.93, -9.01) * mm});
            skArc(sketch, "E259", {"start": v(-8.93, -9.01) * mm, "mid": v(-8.77, -8.67) * mm, "end": v(-8.7, -8.3) * mm});
            skArc(sketch, "E260", {"start": v(-8.7, -8.3) * mm, "mid": v(-8.9, -7.82) * mm, "end": v(-9.22, -7.4) * mm});
            skArc(sketch, "E261", {"start": v(-9.91, -6.59) * mm, "mid": v(-9.57, -7) * mm, "end": v(-9.22, -7.4) * mm});
            skArc(sketch, "E262", {"start": v(-10.32, -5.08) * mm, "mid": v(-10.27, -5.87) * mm, "end": v(-9.91, -6.59) * mm});
            skArc(sketch, "E263", {"start": v(-10.2, -4.7) * mm, "mid": v(-10.27, -4.88) * mm, "end": v(-10.32, -5.08) * mm});
            skArc(sketch, "E264", {"start": v(-9.24, -2.93) * mm, "mid": v(-9.74, -3.8) * mm, "end": v(-10.2, -4.7) * mm});
            skArc(sketch, "E265", {"start": v(-9.24, -2.93) * mm, "mid": v(-9.36, -2.1) * mm, "end": v(-9.7, -1.32) * mm});
            skArc(sketch, "E266", {"start": v(-9.7, -1.32) * mm, "mid": v(-10.82, -0.52) * mm, "end": v(-12.08, 0.04) * mm});
            skArc(sketch, "E267", {"start": v(-12.08, 0.04) * mm, "mid": v(-13.25, 0.4) * mm, "end": v(-14.43, 0.74) * mm});
            skArc(sketch, "E268", {"start": v(-14.43, 0.74) * mm, "mid": v(-15.54, 1.06) * mm, "end": v(-16.64, 1.37) * mm});
            skArc(sketch, "E269", {"start": v(-16.64, 1.37) * mm, "mid": v(-17.68, 1.62) * mm, "end": v(-18.72, 1.81) * mm});
            skArc(sketch, "E270", {"start": v(-18.72, 1.81) * mm, "mid": v(-20.29, 2.12) * mm, "end": v(-21.86, 2.4) * mm});
            skArc(sketch, "E271", {"start": v(-21.86, 2.4) * mm, "mid": v(-23.42, 2.6) * mm, "end": v(-24.99, 2.7) * mm});
            skArc(sketch, "E272", {"start": v(-9.17, -16.68) * mm, "mid": v(-9.1, -15.64) * mm, "end": v(-9.42, -14.65) * mm});
            skArc(sketch, "E273", {"start": v(-10.14, -18.27) * mm, "mid": v(-9.57, -17.53) * mm, "end": v(-9.17, -16.68) * mm});
            skArc(sketch, "E274", {"start": v(-10.14, -18.27) * mm, "mid": v(-10.76, -18.93) * mm, "end": v(-11.36, -19.6) * mm});
            skArc(sketch, "E275", {"start": v(-11.36, -19.6) * mm, "mid": v(-11.66, -20.04) * mm, "end": v(-11.84, -20.55) * mm});
            skLineSegment(sketch, "E276", {"start": v(-11.84, -20.55) * mm, "end": v(-11.73, -21.96) * mm});
            skArc(sketch, "E277", {"start": v(-11.84, -22.7) * mm, "mid": v(-11.75, -22.33) * mm, "end": v(-11.73, -21.96) * mm});
            skArc(sketch, "E278", {"start": v(-13.43, -23.93) * mm, "mid": v(-12.57, -23.4) * mm, "end": v(-11.84, -22.7) * mm});
            skArc(sketch, "E279", {"start": v(-13.43, -23.93) * mm, "mid": v(-13.98, -24.2) * mm, "end": v(-14.52, -24.49) * mm});
            skArc(sketch, "E280", {"start": v(-17.56, -25.07) * mm, "mid": v(-16.02, -24.88) * mm, "end": v(-14.52, -24.49) * mm});
            skArc(sketch, "E281", {"start": v(-20.42, -25.11) * mm, "mid": v(-19, -25.12) * mm, "end": v(-17.56, -25.07) * mm});
            skArc(sketch, "E282", {"start": v(-20.42, -25.11) * mm, "mid": v(-20.54, -25.1) * mm, "end": v(-20.64, -25.13) * mm});
            skArc(sketch, "E283", {"start": v(-20.64, -25.13) * mm, "mid": v(-20.6, -25.27) * mm, "end": v(-20.51, -25.38) * mm});
            skArc(sketch, "E284", {"start": v(-20.51, -25.38) * mm, "mid": v(-19.57, -26.22) * mm, "end": v(-18.37, -26.64) * mm});
            skArc(sketch, "E285", {"start": v(-15.51, -26.8) * mm, "mid": v(-16.94, -26.67) * mm, "end": v(-18.37, -26.64) * mm});
            skArc(sketch, "E286", {"start": v(-14.6, -27.08) * mm, "mid": v(-15.05, -26.9) * mm, "end": v(-15.51, -26.8) * mm});
            skArc(sketch, "E287", {"start": v(-12.82, -28.8) * mm, "mid": v(-13.61, -27.83) * mm, "end": v(-14.6, -27.08) * mm});
            skArc(sketch, "E288", {"start": v(-11.83, -30.5) * mm, "mid": v(-12.3, -29.64) * mm, "end": v(-12.82, -28.8) * mm});
            skArc(sketch, "E289", {"start": v(-11.83, -30.5) * mm, "mid": v(-11.34, -31.37) * mm, "end": v(-10.76, -32.18) * mm});
            skArc(sketch, "E290", {"start": v(-10.76, -32.18) * mm, "mid": v(-10, -32.8) * mm, "end": v(-9.04, -33) * mm});
            skArc(sketch, "E291", {"start": v(-8.08, -32.99) * mm, "mid": v(-8.56, -32.98) * mm, "end": v(-9.04, -33) * mm});
            skArc(sketch, "E292", {"start": v(-8.08, -32.99) * mm, "mid": v(-6.9, -32.66) * mm, "end": v(-5.74, -32.24) * mm});
            skArc(sketch, "E293", {"start": v(-5.74, -32.24) * mm, "mid": v(-4.48, -31.66) * mm, "end": v(-3.25, -31.02) * mm});
            skArc(sketch, "E294", {"start": v(-3.25, -31.02) * mm, "mid": v(-2.26, -30.12) * mm, "end": v(-1.4, -29.1) * mm});
            skArc(sketch, "E295", {"start": v(-1.4, -29.1) * mm, "mid": v(-1.02, -28.52) * mm, "end": v(-0.74, -27.89) * mm});
            skArc(sketch, "E296", {"start": v(-0.74, -27.89) * mm, "mid": v(-0.45, -27.21) * mm, "end": v(-0.25, -26.5) * mm});
            skArc(sketch, "E297", {"start": v(0.06, -25.2) * mm, "mid": v(-0.1, -25.85) * mm, "end": v(-0.25, -26.5) * mm});
            skArc(sketch, "E298", {"start": v(0.06, -25.2) * mm, "mid": v(0.08, -24.22) * mm, "end": v(0.04, -23.24) * mm});
            skArc(sketch, "E299", {"start": v(0.04, -23.24) * mm, "mid": v(-0.3, -21.74) * mm, "end": v(-1.01, -20.37) * mm});
            skArc(sketch, "E300", {"start": v(-1.01, -20.37) * mm, "mid": v(-1.56, -19.65) * mm, "end": v(-2.33, -19.17) * mm});
            skArc(sketch, "E301", {"start": v(-2.33, -19.17) * mm, "mid": v(-2.92, -18.95) * mm, "end": v(-3.52, -18.76) * mm});
            skArc(sketch, "E302", {"start": v(-6.2, -17.42) * mm, "mid": v(-4.95, -18.28) * mm, "end": v(-3.52, -18.76) * mm});
            skArc(sketch, "E303", {"start": v(-9.42, -14.65) * mm, "mid": v(-7.92, -16.16) * mm, "end": v(-6.2, -17.42) * mm});
            skLineSegment(sketch, "E304", {"start": v(-6.15, 8.7) * mm, "end": v(-8.35, 8.57) * mm});
            skLineSegment(sketch, "E305", {"start": v(-8.35, 8.57) * mm, "end": v(-8.47, 10.58) * mm});
            skLineSegment(sketch, "E306", {"start": v(-8.47, 10.58) * mm, "end": v(-6.27, 10.7) * mm});
            skLineSegment(sketch, "E307", {"start": v(-6.27, 10.7) * mm, "end": v(-6.15, 8.7) * mm});
            skCircle(sketch, "E308", {"center": v(-6.4, -6.24) * mm, "radius": 30.85 * mm});
            skCircle(sketch, "E309", {"center": v(-6.4, -6.24) * mm, "radius": 32 * mm});
            skSolve(sketch);
        }
        {
            var Q0;
            Q0 = qSketchRegion(id + "F0", true);
            extrude(context, id + "F1", {"entities" : qUnion([Q0]), "depth" : 25 * mm});
        }
    });
